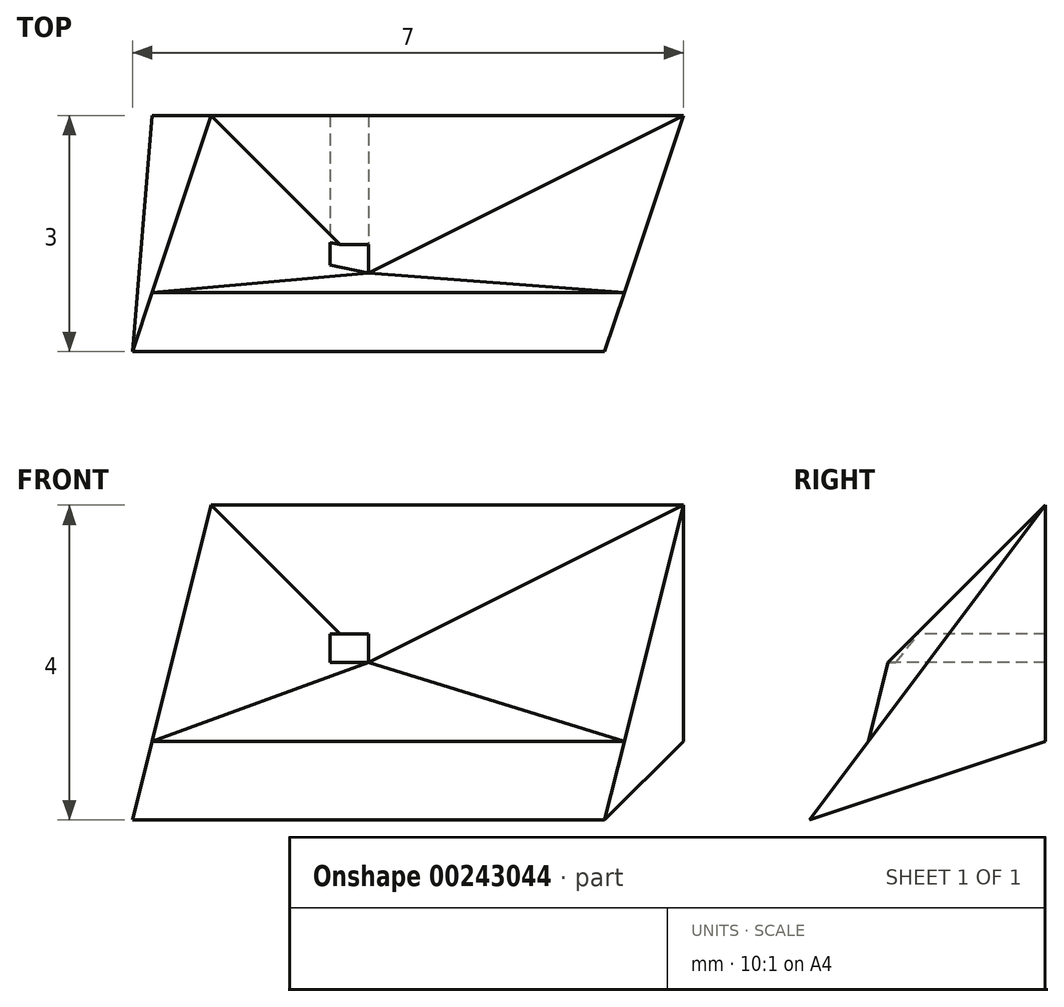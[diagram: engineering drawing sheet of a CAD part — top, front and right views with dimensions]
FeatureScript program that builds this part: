
annotation { "Feature Type Name" : "Feature", "Feature Type Description" : "" }
export const myFeature = defineFeature(function(context is Context, id is Id, definition is map)
    precondition{}
    {
        {
            var Q0;
            Q0=qCreatedBy(makeId("Top.planeOp"),FACE);
            var sketch = newSketch(context, id + "F0", { "sketchPlane" : qUnion([Q0])});
            skLineSegment(sketch, "E0.bottom", {"start": v(0, 0) * mm, "end": v(7, 0) * mm});
            skLineSegment(sketch, "E0.top", {"start": v(0, 3) * mm, "end": v(7, 3) * mm});
            skLineSegment(sketch, "E0.left", {"start": v(0, 0) * mm, "end": v(0, 3) * mm});
            skLineSegment(sketch, "E0.right", {"start": v(7, 0) * mm, "end": v(7, 3) * mm});
            skSolve(sketch);
        }
        {
            var Q0;
            Q0 = qSketchRegion(id + "F0", true);
            extrude(context, id + "F1", {"entities" : qUnion([Q0]), "depth" : 4 * mm});
        }
        {
            var Q0;
            Q0=makeQuery(id+"F1.opExtrude","SWEPT_FACE",FACE,{"disambiguationData":[OSD([sQuery(id+"F0.wireOp",EDGE,"E0.bottom")])]});
            var sketch = newSketch(context, id + "F2", { "sketchPlane" : qUnion([Q0])});
            skLineSegment(sketch, "E1", {"start": v(7, 0) * mm, "end": v(6, 0) * mm, "construction": true});
            skLineSegment(sketch, "E2", {"start": v(0, 4) * mm, "end": v(3, 4) * mm, "construction": true});
            skLineSegment(sketch, "E3", {"start": v(3, 4) * mm, "end": v(3, 2) * mm, "construction": true});
            skLineSegment(sketch, "E4.bottom", {"start": v(3, 2) * mm, "end": v(2.5, 2) * mm});
            skLineSegment(sketch, "E4.top", {"start": v(3, 2.36) * mm, "end": v(2.5, 2.36) * mm});
            skLineSegment(sketch, "E4.left", {"start": v(3, 2) * mm, "end": v(3, 2.36) * mm});
            skLineSegment(sketch, "E4.right", {"start": v(2.5, 2) * mm, "end": v(2.5, 2.36) * mm});
            skSolve(sketch);
        }
        {
            var Q0;
            Q0=makeQuery(id+"F1.opExtrude","SWEPT_FACE",FACE,{"disambiguationData":[OSD([sQuery(id+"F0.wireOp",EDGE,"E0.top")])]});
            var sketch = newSketch(context, id + "F3", { "sketchPlane" : qUnion([Q0])});
            skLineSegment(sketch, "E5", {"start": v(0, 4) * mm, "end": v(-1, 4) * mm, "construction": true});
            skSolve(sketch);
        }
        {
            var Q0;
            Q0=sQuery(id+"F3.wireOp",VERTEX,"E5.end");
            var Q1;
            Q1=sQuery(id+"F2.wireOp",VERTEX,"E1.end");
            var Q2;
            Q2=makeQuery(id+"F1.opExtrude","CAP_VERTEX",VERTEX,{"disambiguationData":[OSD([sQuery(id+"F0.wireOp",EDGE,"E0.top"),sQuery(id+"F0.wireOp",EDGE,"E0.right")])],"isStart":false});
            cPlane(context, id + "F4", {"entities" : qUnion([Q0, Q1, Q2]), "cplaneType" : CPlaneType.THREE_POINT, "offset" : 25 * mm, "width" : 150 * mm, "height" : 150 * mm});
        }
        {
            var Q0;
            Q0=qCreatedBy(id+"F4.planeOp",FACE);
            var sketch = newSketch(context, id + "F5", { "sketchPlane" : qUnion([Q0])});
            skPoint(sketch, "E6.0", {"position": v(-7, 5) * mm});
            skLineSegment(sketch, "E7.bottom", {"start": v(0, 0) * mm, "end": v(-7, 0) * mm});
            skLineSegment(sketch, "E7.top", {"start": v(0, 5) * mm, "end": v(-7, 5) * mm});
            skLineSegment(sketch, "E7.left", {"start": v(0, 0) * mm, "end": v(0, 5) * mm});
            skLineSegment(sketch, "E7.right", {"start": v(-7, 0) * mm, "end": v(-7, 5) * mm});
            skSolve(sketch);
        }
        {
            var Q0;
            Q0 = qSketchRegion(id + "F5", true);
            extrude(context, id + "F6", {"entities" : qUnion([Q0]), "operationType" : NewBodyOperationType.REMOVE, "oppositeDirection" : true, "depth" : 25 * mm});
        }
        {
            var Q0;
            Q0=makeQuery(id+"F6.boolean.opBoolean","MERGE",VERTEX,{"derivedFrom":[makeQuery(id+"F1.opExtrude","CAP_VERTEX",VERTEX,{"disambiguationData":[OSD([sQuery(id+"F0.wireOp",EDGE,"E0.top"),sQuery(id+"F0.wireOp",EDGE,"E0.right")])],"isStart":false}),makeQuery(id+"F6.opExtrude","CAP_VERTEX",VERTEX,{"disambiguationData":[OSD([sQuery(id+"F5.wireOp",EDGE,"E7.top"),sQuery(id+"F5.wireOp",EDGE,"E7.right")])],"isStart":true})]});
            var Q1;
            Q1=sQuery(id+"F2.wireOp",VERTEX,"E1.end");
            var Q2;
            Q2=makeQuery(id+"F1.opExtrude","CAP_VERTEX",VERTEX,{"disambiguationData":[OSD([sQuery(id+"F0.wireOp",EDGE,"E0.top"),sQuery(id+"F0.wireOp",EDGE,"E0.right")])],"isStart":true});
            cPlane(context, id + "F7", {"entities" : qUnion([Q0, Q1, Q2]), "cplaneType" : CPlaneType.THREE_POINT, "offset" : 25 * mm, "width" : 150 * mm, "height" : 150 * mm});
        }
        {
            var Q0;
            Q0=qCreatedBy(id+"F7.planeOp",FACE);
            var sketch = newSketch(context, id + "F8", { "sketchPlane" : qUnion([Q0])});
            skPoint(sketch, "E8.0", {"position": v(-5.06, 4) * mm});
            skPoint(sketch, "E9.0", {"position": v(-5.06, 0) * mm});
            skPoint(sketch, "E10.0", {"position": v(-1.9, 0) * mm});
            skLineSegment(sketch, "E11", {"start": v(-5.06, 4) * mm, "end": v(-1.9, 0) * mm});
            skLineSegment(sketch, "E12", {"start": v(-5.06, 0) * mm, "end": v(-1.9, 0) * mm});
            skLineSegment(sketch, "E13", {"start": v(-5.06, 4) * mm, "end": v(-5.06, 0) * mm});
            skLineSegment(sketch, "E14", {"start": v(-5.06, 0) * mm, "end": v(-5.06, 1) * mm});
            skSolve(sketch);
        }
        {
            var Q0;
            Q0 = qSketchRegion(id + "F8", true);
            extrude(context, id + "F9", {"entities" : qUnion([Q0]), "operationType" : NewBodyOperationType.REMOVE, "oppositeDirection" : true, "depth" : 25 * mm});
        }
        {
            var Q0;
            Q0=sQuery(id+"F3.wireOp",VERTEX,"E5.end");
            var Q1;
            Q1=qCreatedBy(makeId("Origin.pointOp"),VERTEX);
            var Q2;
            Q2=makeQuery(id+"F1.opExtrude","CAP_VERTEX",VERTEX,{"disambiguationData":[OSD([sQuery(id+"F0.wireOp",EDGE,"E0.top"),sQuery(id+"F0.wireOp",EDGE,"E0.left")])],"isStart":true});
            cPlane(context, id + "F10", {"entities" : qUnion([Q0, Q1, Q2]), "cplaneType" : CPlaneType.THREE_POINT, "offset" : 25 * mm, "width" : 150 * mm, "height" : 150 * mm});
        }
        {
            var Q0;
            Q0=qCreatedBy(id+"F10.planeOp",FACE);
            var sketch = newSketch(context, id + "F11", { "sketchPlane" : qUnion([Q0])});
            skPoint(sketch, "E15.0", {"position": v(-3, 4.12) * mm});
            skPoint(sketch, "E16.0", {"position": v(-3, 0) * mm});
            skLineSegment(sketch, "E17", {"start": v(-3, 4.12) * mm, "end": v(0, 0) * mm});
            skLineSegment(sketch, "E18", {"start": v(0, 0) * mm, "end": v(-3, 0) * mm});
            skLineSegment(sketch, "E19", {"start": v(-3, 4.12) * mm, "end": v(-3, 0) * mm});
            skSolve(sketch);
        }
        {
            var Q0;
            Q0 = qSketchRegion(id + "F11", true);
            extrude(context, id + "F12", {"entities" : qUnion([Q0]), "operationType" : NewBodyOperationType.REMOVE, "depth" : 25 * mm});
        }
        {
            var Q0;
            {var subQ0=sQuery(id+"F0.wireOp",EDGE,"E0.top");Q0=makeQuery(id+"F3.imprint","IMPRINT",FACE,{"disambiguationData":[TD([[makeQuery(id+"F3.imprint","IMPRINT",EDGE,{"derivedFrom":makeQuery(id+"F1.opExtrude","CAP_EDGE",EDGE,{"disambiguationData":[OSD([subQ0])],"isStart":true})}),-1.0]])]});}
            var sketch = newSketch(context, id + "F13", { "sketchPlane" : qUnion([Q0])});
            skLineSegment(sketch, "E20", {"start": v(0, 0) * mm, "end": v(0, 1) * mm, "construction": true});
            skLineSegment(sketch, "E21.0", {"start": v(-7, 4) * mm, "end": v(-7, 0) * mm});
            skLineSegment(sketch, "E22.0.0", {"start": v(-7, 0) * mm, "end": v(0, 0) * mm});
            skLineSegment(sketch, "E22.0.1", {"start": v(0, 0) * mm, "end": v(0, 4) * mm});
            skLineSegment(sketch, "E22.0.2", {"start": v(0, 4) * mm, "end": v(-7, 4) * mm});
            skPoint(sketch, "E23.0", {"position": v(-7, 0) * mm});
            skLineSegment(sketch, "E24", {"start": v(0, 1) * mm, "end": v(-7, 1) * mm, "construction": true});
            skSolve(sketch);
        }
        {
            var Q0;
            Q0=sQuery(id+"F13.wireOp",VERTEX,"E24.end");
            var Q1;
            Q1=sQuery(id+"F8.wireOp",VERTEX,"E10.0");
            var Q2;
            Q2=sQuery(id+"F13.wireOp",VERTEX,"E20.end");
            cPlane(context, id + "F14", {"entities" : qUnion([Q0, Q1, Q2]), "cplaneType" : CPlaneType.THREE_POINT, "offset" : 25 * mm, "width" : 150 * mm, "height" : 150 * mm});
        }
        {
            var Q0;
            Q0=qCreatedBy(id+"F14.planeOp",FACE);
            var sketch = newSketch(context, id + "F15", { "sketchPlane" : qUnion([Q0])});
            skLineSegment(sketch, "E25.bottom", {"start": v(8.59, 3.83) * mm, "end": v(-2.3, 3.83) * mm});
            skLineSegment(sketch, "E25.top", {"start": v(8.59, -1.16) * mm, "end": v(-2.3, -1.16) * mm});
            skLineSegment(sketch, "E25.left", {"start": v(8.59, 3.83) * mm, "end": v(8.59, -1.16) * mm});
            skLineSegment(sketch, "E25.right", {"start": v(-2.3, 3.83) * mm, "end": v(-2.3, -1.16) * mm});
            skSolve(sketch);
        }
        {
            var Q0;
            Q0 = qSketchRegion(id + "F15", true);
            extrude(context, id + "F16", {"entities" : qUnion([Q0]), "operationType" : NewBodyOperationType.REMOVE, "oppositeDirection" : true, "depth" : 25 * mm});
        }
        {
            var Q0;
            Q0=makeQuery(id+"F6.boolean.opBoolean","COPY",FACE,{"derivedFrom":makeQuery(id+"F6.opExtrude","CAP_FACE",FACE,{"disambiguationData":[OSD([sQuery(id+"F5.wireOp",EDGE,"E7.bottom"),sQuery(id+"F5.wireOp",EDGE,"E7.top"),sQuery(id+"F5.wireOp",EDGE,"E7.left"),sQuery(id+"F5.wireOp",EDGE,"E7.right")])],"isStart":true})});
            var sketch = newSketch(context, id + "F17", { "sketchPlane" : qUnion([Q0])});
            skLineSegment(sketch, "E26", {"start": v(0, 0) * mm, "end": v(0, 1.25) * mm, "construction": true});
            skLineSegment(sketch, "E27", {"start": v(0, 1.25) * mm, "end": v(6.25, 1.25) * mm});
            skPoint(sketch, "E28.0", {"position": v(1, 5) * mm});
            skPoint(sketch, "E29.0", {"position": v(7, 5) * mm});
            skPoint(sketch, "E30", {"position": v(0.25, 1.25) * mm});
            skSolve(sketch);
        }
        {
            var Q0;
            Q0 = qSketchRegion(id + "F2", true);
            extrude(context, id + "F18", {"entities" : qUnion([Q0]), "operationType" : NewBodyOperationType.ADD, "oppositeDirection" : true, "depth" : 1 * mm});
        }
        {
            var Q0;
            Q0=makeQuery(id+"F18.opExtrude","CAP_VERTEX",VERTEX,{"disambiguationData":[OSD([sQuery(id+"F2.wireOp",EDGE,"E4.bottom"),sQuery(id+"F2.wireOp",EDGE,"E4.left")])],"isStart":false});
            var Q1;
            Q1=sQuery(id+"F17.wireOp",VERTEX,"E27.end");
            var Q2;
            Q2=sQuery(id+"F17.wireOp",VERTEX,"E30");
            cPlane(context, id + "F19", {"entities" : qUnion([Q0, Q1, Q2]), "cplaneType" : CPlaneType.THREE_POINT, "offset" : 25 * mm, "width" : 150 * mm, "height" : 150 * mm});
        }
        {
            var Q0;
            Q0=qCreatedBy(id+"F19.planeOp",FACE);
            var sketch = newSketch(context, id + "F20", { "sketchPlane" : qUnion([Q0])});
            skPoint(sketch, "E31.0", {"position": v(3, 2.18) * mm});
            skPoint(sketch, "E32.0", {"position": v(6.25, 1.15) * mm});
            skPoint(sketch, "E33.0", {"position": v(0.25, 1.15) * mm});
            skLineSegment(sketch, "E34", {"start": v(0.25, 1.15) * mm, "end": v(3, 2.18) * mm});
            skLineSegment(sketch, "E35", {"start": v(6.25, 1.15) * mm, "end": v(3, 2.18) * mm});
            skLineSegment(sketch, "E36", {"start": v(0.25, 1.15) * mm, "end": v(6.25, 1.15) * mm});
            skSolve(sketch);
        }
        {
            var Q1;
            Q1 = qSketchRegion(id + "F20", true);
            var Q2;
            Q2=sQuery(id+"F17.wireOp",VERTEX,"E28.0");
            loft(context, id + "F21", {"operationType" : NewBodyOperationType.ADD, "sheetProfilesArray" : [{ "sheetProfileEntities" : qUnion([Q1]) }, { "sheetProfileEntities" : qUnion([Q2]) }]});
        }
        {
            var Q0;
            Q0=makeQuery(id+"F18.opExtrude","CAP_VERTEX",VERTEX,{"disambiguationData":[OSD([sQuery(id+"F2.wireOp",EDGE,"E4.bottom"),sQuery(id+"F2.wireOp",EDGE,"E4.left")])],"isStart":false});
            var Q1;
            Q1=sQuery(id+"F17.wireOp",VERTEX,"E27.end");
            var Q2;
            Q2=sQuery(id+"F5.wireOp",VERTEX,"E6.0");
            cPlane(context, id + "F22", {"entities" : qUnion([Q0, Q1, Q2]), "cplaneType" : CPlaneType.THREE_POINT, "offset" : 25 * mm, "width" : 150 * mm, "height" : 150 * mm});
        }
        {
            var Q0;
            Q0=qCreatedBy(id+"F22.planeOp",FACE);
            var sketch = newSketch(context, id + "F23", { "sketchPlane" : qUnion([Q0])});
            skPoint(sketch, "E37.0", {"position": v(-2.94, 2.2) * mm});
            skPoint(sketch, "E38.0", {"position": v(-6.21, 1.25) * mm});
            skPoint(sketch, "E39.0", {"position": v(-6.97, 5) * mm});
            skLineSegment(sketch, "E40", {"start": v(-2.94, 2.2) * mm, "end": v(-6.21, 1.25) * mm});
            skLineSegment(sketch, "E41", {"start": v(-6.21, 1.25) * mm, "end": v(-6.97, 5) * mm});
            skLineSegment(sketch, "E42", {"start": v(-6.97, 5) * mm, "end": v(-2.94, 2.2) * mm});
            skSolve(sketch);
        }
        {
            var Q1;
            Q1 = qSketchRegion(id + "F23", true);
            var Q2;
            Q2=sQuery(id+"F17.wireOp",VERTEX,"E28.0");
            loft(context, id + "F24", {"operationType" : NewBodyOperationType.ADD, "sheetProfilesArray" : [{ "sheetProfileEntities" : qUnion([Q1]) }, { "sheetProfileEntities" : qUnion([Q2]) }]});
        }
        {
            var Q0;
            Q0=makeQuery(id+"F18.opExtrude","CAP_FACE",FACE,{"disambiguationData":[OSD([sQuery(id+"F2.wireOp",EDGE,"E4.bottom"),sQuery(id+"F2.wireOp",EDGE,"E4.top"),sQuery(id+"F2.wireOp",EDGE,"E4.left"),sQuery(id+"F2.wireOp",EDGE,"E4.right")])],"isStart":true});
            extrude(context, id + "F25", {"entities" : qUnion([Q0]), "operationType" : NewBodyOperationType.REMOVE, "oppositeDirection" : true, "depth" : 25 * mm});
        }
    });
